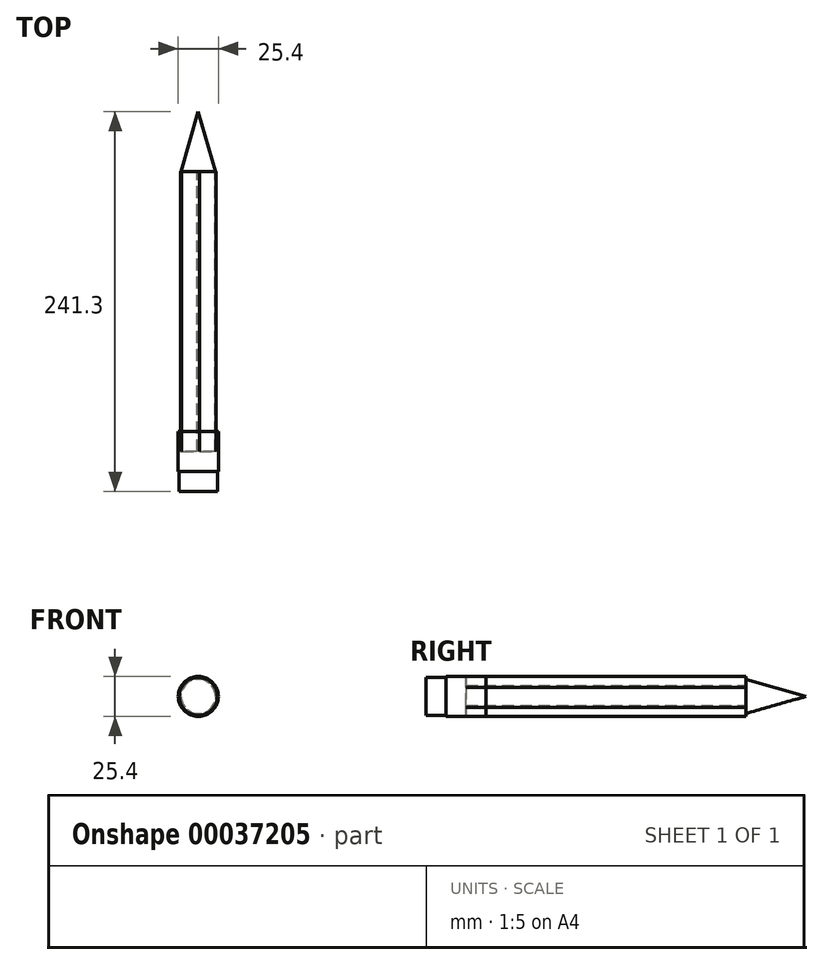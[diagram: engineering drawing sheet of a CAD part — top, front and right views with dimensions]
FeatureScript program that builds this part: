
annotation { "Feature Type Name" : "Feature", "Feature Type Description" : "" }
export const myFeature = defineFeature(function(context is Context, id is Id, definition is map)
    precondition{}
    {
        {
            var Q0;
            Q0=qCreatedBy(makeId("Front.planeOp"),FACE);
            var sketch = newSketch(context, id + "F0", { "sketchPlane" : qUnion([Q0])});
            skCircle(sketch, "E0.cCircle", {"center": v(0, 0) * mm, "radius": 11 * mm, "construction": true});
            skLineSegment(sketch, "E0.0", {"start": v(10.6, -7) * mm, "end": v(-0.77, -12.68) * mm});
            skLineSegment(sketch, "E0.1", {"start": v(-0.77, -12.68) * mm, "end": v(-11.36, -5.67) * mm});
            skLineSegment(sketch, "E0.2", {"start": v(-11.36, -5.67) * mm, "end": v(-10.6, 7) * mm});
            skLineSegment(sketch, "E0.3", {"start": v(-10.6, 7) * mm, "end": v(0.77, 12.68) * mm});
            skLineSegment(sketch, "E0.4", {"start": v(0.77, 12.68) * mm, "end": v(11.36, 5.67) * mm});
            skLineSegment(sketch, "E0.5", {"start": v(11.36, 5.67) * mm, "end": v(10.6, -7) * mm});
            skPoint(sketch, "E0.0.midPoint", {"position": v(4.91, -9.84) * mm});
            skPoint(sketch, "E1", {"position": v(10.98, -0.67) * mm});
            skSolve(sketch);
        }
        {
            var Q0;
            Q0 = qSketchRegion(id + "F0", true);
            extrude(context, id + "F1", {"entities" : qUnion([Q0]), "depth" : 177.8 * mm});
        }
        {
            var Q0;
            Q0=qCreatedBy(makeId("Top.planeOp"),FACE);
            var sketch = newSketch(context, id + "F2", { "sketchPlane" : qUnion([Q0])});
            skLineSegment(sketch, "E2", {"start": v(0, 0) * mm, "end": v(10.92, 0) * mm});
            skLineSegment(sketch, "E3", {"start": v(0, 0) * mm, "end": v(0, 38.1) * mm});
            skLineSegment(sketch, "E4", {"start": v(0, 38.1) * mm, "end": v(10.92, 0) * mm});
            skSolve(sketch);
        }
        {
            var Q0;
            Q0 = qSketchRegion(id + "F2", true);
            var Q1;
            Q1=sQuery(id+"F2.wireOp",EDGE,"E3");
            revolve(context, id + "F3", {"operationType" : NewBodyOperationType.ADD, "entities" : qUnion([Q0]), "axis" : qUnion([Q1]), "revolveType" : RevolveType.FULL});
        }
        {
            var Q0;
            Q0=makeQuery(id+"F1.opExtrude","CAP_FACE",FACE,{"disambiguationData":[OSD([sQuery(id+"F0.wireOp",EDGE,"E0.0"),sQuery(id+"F0.wireOp",EDGE,"E0.1"),sQuery(id+"F0.wireOp",EDGE,"E0.2"),sQuery(id+"F0.wireOp",EDGE,"E0.3"),sQuery(id+"F0.wireOp",EDGE,"E0.4"),sQuery(id+"F0.wireOp",EDGE,"E0.5")])],"isStart":false});
            var sketch = newSketch(context, id + "F4", { "sketchPlane" : qUnion([Q0])});
            skCircle(sketch, "E5", {"center": v(0, 0) * mm, "radius": 12.7 * mm});
            skSolve(sketch);
        }
        {
            var Q0;
            Q0 = qSketchRegion(id + "F4", true);
            extrude(context, id + "F5", {"entities" : qUnion([Q0]), "endBound" : BoundingType.SYMMETRIC, "depth" : 25.4 * mm});
        }
        {
            var Q0;
            Q0=makeQuery(id+"F5.opExtrude","CAP_FACE",FACE,{"disambiguationData":[OSD([sQuery(id+"F4.wireOp",EDGE,"E5")])],"isStart":false});
            var sketch = newSketch(context, id + "F6", { "sketchPlane" : qUnion([Q0])});
            skCircle(sketch, "E6", {"center": v(0, 0) * mm, "radius": 12.1 * mm});
            skSolve(sketch);
        }
        {
            var Q0;
            Q0 = qSketchRegion(id + "F6", true);
            extrude(context, id + "F7", {"entities" : qUnion([Q0]), "depth" : 12.7 * mm});
        }
    });
